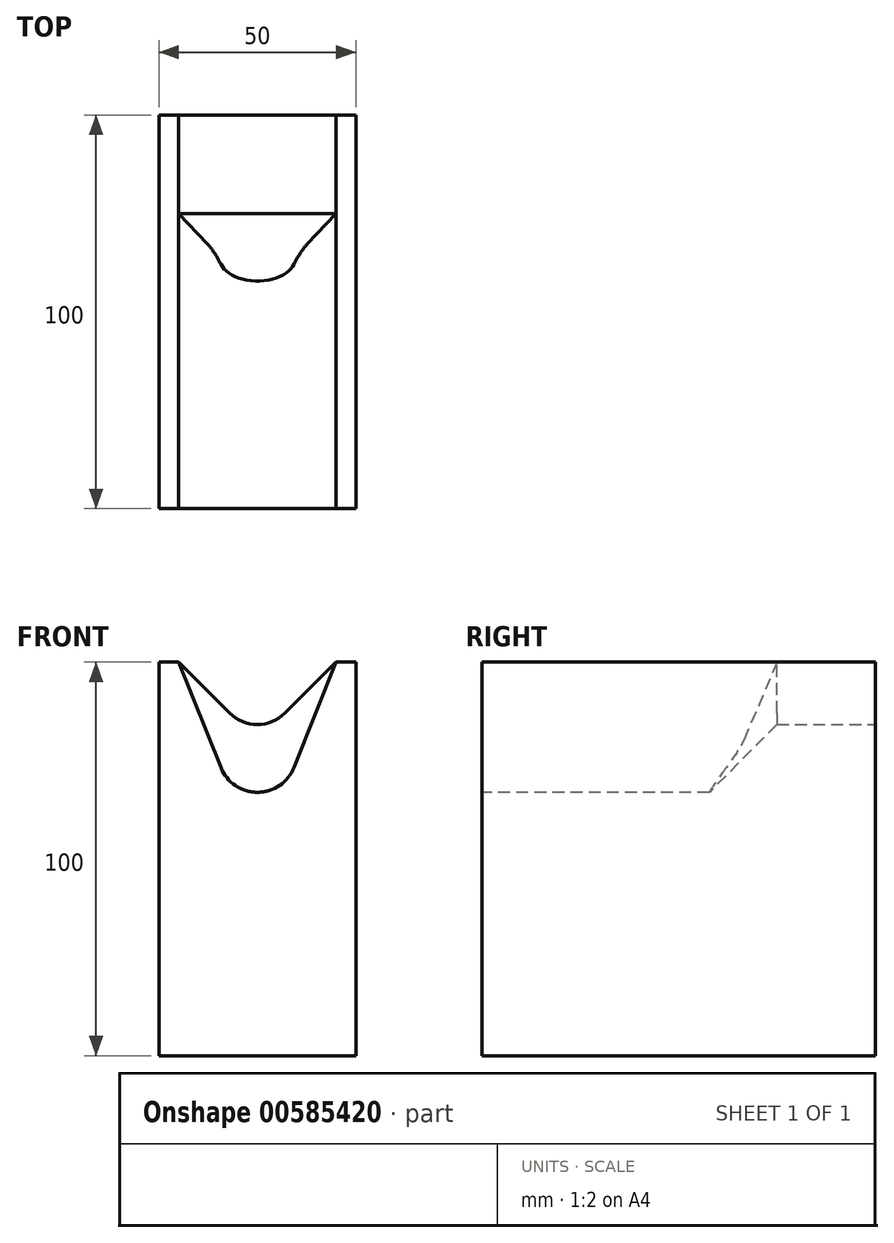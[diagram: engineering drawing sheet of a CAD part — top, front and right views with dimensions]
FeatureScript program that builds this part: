
annotation { "Feature Type Name" : "Feature", "Feature Type Description" : "" }
export const myFeature = defineFeature(function(context is Context, id is Id, definition is map)
    precondition{}
    {
        {
            var Q0;
            Q0=qCreatedBy(makeId("Top.planeOp"),FACE);
            var sketch = newSketch(context, id + "F0", { "sketchPlane" : qUnion([Q0])});
            skLineSegment(sketch, "E0.bottom", {"start": v(-35.27, 84.56) * mm, "end": v(14.73, 84.56) * mm});
            skLineSegment(sketch, "E0.top", {"start": v(-35.27, -15.44) * mm, "end": v(14.73, -15.44) * mm});
            skLineSegment(sketch, "E0.left", {"start": v(-35.27, 84.56) * mm, "end": v(-35.27, -15.44) * mm});
            skLineSegment(sketch, "E0.right", {"start": v(14.73, 84.56) * mm, "end": v(14.73, -15.44) * mm});
            skSolve(sketch);
        }
        {
            var Q0;
            Q0=makeQuery(id+"F0.imprint","IMPRINT",FACE,{"disambiguationData":[TD([[makeQuery(id+"F0.imprint","IMPRINT",EDGE,{"derivedFrom":sQuery(id+"F0.wireOp",EDGE,"E0.bottom")}),-1.0]])]});
            extrude(context, id + "F1", {"entities" : qUnion([Q0]), "depth" : 100 * mm, "offsetDistance" : 25 * mm});
        }
        {
            var Q0;
            Q0=makeQuery(id+"F1.opExtrude","SWEPT_FACE",FACE,{"disambiguationData":[OSD([sQuery(id+"F0.wireOp",EDGE,"E0.top")])]});
            var sketch = newSketch(context, id + "F2", { "sketchPlane" : qUnion([Q0])});
            skLineSegment(sketch, "E1", {"start": v(-35.27, 100) * mm, "end": v(-30.27, 100) * mm});
            skLineSegment(sketch, "E2", {"start": v(14.73, 100) * mm, "end": v(9.73, 100) * mm});
            skPoint(sketch, "E2.endSnap0", {"position": v(-32.77, 100) * mm});
            skLineSegment(sketch, "E3", {"start": v(9.73, 100) * mm, "end": v(-0.99, 73.21) * mm});
            skPoint(sketch, "E3.endSnap0", {"position": v(-10.27, 0) * mm});
            skLineSegment(sketch, "E4", {"start": v(-19.55, 73.21) * mm, "end": v(-30.27, 100) * mm});
            skPoint(sketch, "E5.visualSharp", {"position": v(-10.27, 50) * mm});
            skArc(sketch, "E5.filletArc", {"start": v(-19.55, 73.21) * mm, "mid": v(-10.27, 66.93) * mm, "end": v(-0.99, 73.21) * mm});
            skSolve(sketch);
        }
        {
            var Q0;
            Q0=makeQuery(id+"F1.opExtrude","SWEPT_FACE",FACE,{"disambiguationData":[OSD([sQuery(id+"F0.wireOp",EDGE,"E0.bottom")])]});
            var sketch = newSketch(context, id + "F3", { "sketchPlane" : qUnion([Q0])});
            skLineSegment(sketch, "E6", {"start": v(-14.73, 100) * mm, "end": v(-9.73, 100) * mm});
            skLineSegment(sketch, "E7", {"start": v(35.27, 100) * mm, "end": v(30.27, 100) * mm});
            skLineSegment(sketch, "E8", {"start": v(-9.73, 100) * mm, "end": v(3.2, 87.07) * mm});
            skPoint(sketch, "E8.endSnap0", {"position": v(10.27, 0) * mm});
            skLineSegment(sketch, "E9", {"start": v(17.34, 87.07) * mm, "end": v(30.27, 100) * mm});
            skPoint(sketch, "E10.visualSharp", {"position": v(10.27, 80) * mm});
            skArc(sketch, "E10.filletArc", {"start": v(3.2, 87.07) * mm, "mid": v(10.27, 84.14) * mm, "end": v(17.34, 87.07) * mm});
            skSolve(sketch);
        }
        {
            var Q0;
            {var subQ0=sQuery(id+"F2.wireOp",EDGE,"E3");Q0=makeQuery(id+"F2.imprint","IMPRINT",FACE,{"disambiguationData":[TD([[makeQuery(id+"F2.imprint","IMPRINT",EDGE,{"derivedFrom":subQ0}),-1.0]])]});}
            extrude(context, id + "F4", {"entities" : qUnion([Q0]), "operationType" : NewBodyOperationType.REMOVE, "oppositeDirection" : true, "depth" : 50 * mm, "offsetDistance" : 25 * mm});
        }
        {
            var Q0;
            {var subQ0=sQuery(id+"F3.wireOp",EDGE,"E8");Q0=makeQuery(id+"F3.imprint","IMPRINT",FACE,{"disambiguationData":[TD([[makeQuery(id+"F3.imprint","IMPRINT",EDGE,{"derivedFrom":subQ0}),1.0]])]});}
            extrude(context, id + "F5", {"entities" : qUnion([Q0]), "operationType" : NewBodyOperationType.REMOVE, "oppositeDirection" : true, "depth" : 126 * mm, "offsetDistance" : 25 * mm});
        }
        {
            var Q0;
            Q0=makeQuery(id+"F5.boolean.opBoolean","INTERSECT",EDGE,{"derivedFrom":[makeQuery(id+"F4.boolean.opBoolean","COPY",FACE,{"derivedFrom":makeQuery(id+"F4.opExtrude","CAP_FACE",FACE,{"disambiguationData":[OSD([sQuery(id+"F0.wireOp",EDGE,"E0.top"),sQuery(id+"F2.wireOp",EDGE,"E3"),sQuery(id+"F2.wireOp",EDGE,"E4"),sQuery(id+"F2.wireOp",EDGE,"E5.filletArc")])],"isStart":false})}),makeQuery(id+"F5.opExtrude","SWEPT_FACE",FACE,{"disambiguationData":[OSD([sQuery(id+"F3.wireOp",EDGE,"E9")])]})]});
            var Q1;
            Q1=makeQuery(id+"F5.boolean.opBoolean","INTERSECT",EDGE,{"derivedFrom":[makeQuery(id+"F4.boolean.opBoolean","COPY",FACE,{"derivedFrom":makeQuery(id+"F4.opExtrude","CAP_FACE",FACE,{"disambiguationData":[OSD([sQuery(id+"F0.wireOp",EDGE,"E0.top"),sQuery(id+"F2.wireOp",EDGE,"E3"),sQuery(id+"F2.wireOp",EDGE,"E4"),sQuery(id+"F2.wireOp",EDGE,"E5.filletArc")])],"isStart":false})}),makeQuery(id+"F5.opExtrude","SWEPT_FACE",FACE,{"disambiguationData":[OSD([sQuery(id+"F3.wireOp",EDGE,"E8")])]})]});
            var Q2;
            Q2=makeQuery(id+"F5.boolean.opBoolean","INTERSECT",EDGE,{"derivedFrom":[makeQuery(id+"F4.boolean.opBoolean","COPY",FACE,{"derivedFrom":makeQuery(id+"F4.opExtrude","CAP_FACE",FACE,{"disambiguationData":[OSD([sQuery(id+"F0.wireOp",EDGE,"E0.top"),sQuery(id+"F2.wireOp",EDGE,"E3"),sQuery(id+"F2.wireOp",EDGE,"E4"),sQuery(id+"F2.wireOp",EDGE,"E5.filletArc")])],"isStart":false})}),makeQuery(id+"F5.opExtrude","SWEPT_FACE",FACE,{"disambiguationData":[OSD([sQuery(id+"F3.wireOp",EDGE,"E10.filletArc")])]})]});
            chamfer(context, id + "F6", {"entities" : qUnion([Q0, Q1, Q2]), "width" : 25 * mm, "tangentPropagation" : true});
        }
    });
